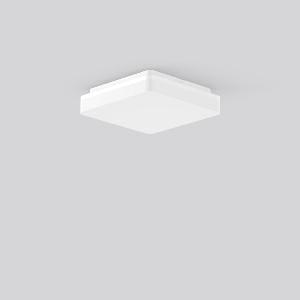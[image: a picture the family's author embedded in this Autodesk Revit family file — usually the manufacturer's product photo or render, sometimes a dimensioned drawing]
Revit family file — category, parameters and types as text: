
# Revit family: hb_506_221188_002_2_899e
name_source: partatom
category: Lighting Fixtures
units: mm (PartAtom-declared; Revit-internal decimal feet)

## family parameters
Cut with Voids When Loaded = No
Host = Face
Light Source = No
Part Type = Normal
Room Calculation Point = No
Round Connector Dimension = Use Diameter
Shared = No

## types (1)
- MultiColor 830 (1 x LED Modul 830, 1350 lm, 3000)
    Apparent Load = 15 VA
    CIE Flux Codes = 42 73 92 89 100
    Color Rendering = 80
    Color Temperature = 3000
    Default Elevation = 1800 mm
    Description = Series: HB 506
Ceiling and wall luminaire with slim design. Housing: plastic (polycarbonate). Diffuser: plastic (polycarbonate), opal. Base and diffuser are sealed together. MultiColour: Colour temperature adjustable via switching element. Choice of 3000 K or 4000 K. Factory setting is 3000 K. Quick mounting adapter galvanized steel sheet, with fastening screws. Driver integrated. 
Colour: white
Length: 210 mm
Width: 210 mm
Height: 53 mm
Lamp: LED
Socket: without socket
Colour temperature: 3000K, 4000K
Colour rendering index (CRI): 80
System power: 15 W
Rated luminous flux: 1350 lm
Luminous efficiency: 90 lm/W
System power 2: 15 W
Rated luminous flux 2: 1400 lm
Luminous efficiency 2: 93 lm/W
Control gear: EB
Protection class: I
Type of protection: IP 20
    Height = 53 mm
    Lamp = 1 x LED Modul 830
    Lamp Light Flux = 1350 lm
    Lamp count = 1
    Length = 210 mm
    Lifetime = 50000 h
    Luminous efficacy = 90 lm/W
    Manufacturer = RZB
    ModVariant = No
    Model = 221188.002.2
    Mounting Place = Ceiling, Wall
    Mounting Type = Surface mounted
    Number of Poles = 1
    OnlyDefault = Yes
    Power Factor = 1
    Product Name = HB 506
    Product group = Surface mounted ceiling and wall luminaires
    ProductGroupID = 305
    Protection Class = Protection class I
    Protection Degree = IP 20
    RLX_Detail_Level = 1
    RLX_Emergency_Light_Flux = 0 lm
    RLX_Emergency_Type = 0
    RLX_Emergency_Type_DB = No
    RlxData = <blob elided: 38289 chars, md5=9682faef>
    Socket = socket
    Standby Power = 0 W
    System Light Flux = 1350 lm
    System Power = 15 W
    Type Comments = MultiColor 830
    Type Image = 221188.002.jpg
    URL = http://relux.com
    VarID = multicolor_830
    Voltage = 230 V
    Voltage Range = 220-240 V
    Weight = 0.00 kg
    Width = 210 mm

## geometry (parser evidence)
native form markers: Blend x4, Sweep x10
no freeform markers — native parametric forms only
